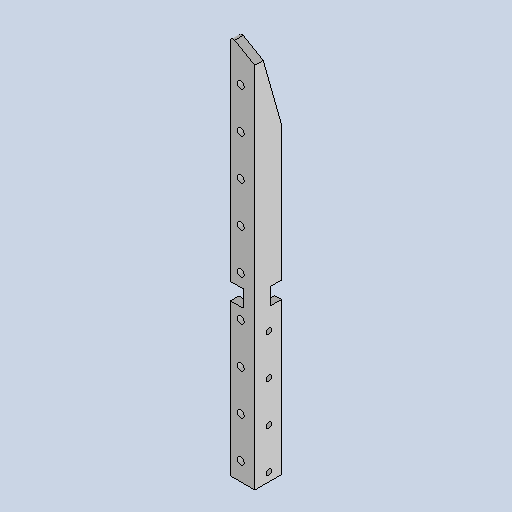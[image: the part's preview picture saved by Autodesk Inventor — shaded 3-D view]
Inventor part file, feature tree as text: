
AUTODESK INVENTOR PART (.ipt)
format: ipt  version: 2025 (Build 290162010, 162A)  size: 134,656 bytes
history: native  units: mm
features: sketch x6, other x3
ambient origin geometry x8: Origin, YZ Plane, XZ Plane, XY Plane, X Axis, Y Axis, Z Axis, Center Point
bodies: Solid1 (feature_tree)
feature tree (9):
  other  "1013.ipt"
  other  "Solid1::1013.ipt"
  other  "TaggingFeature1"
  sketch  "Sketch1"  dims[d0=10.0mm]
  sketch  "Sketch2"
  sketch  "Sketch3"
  sketch  "Sketch4"
  sketch  "Sketch5"
  sketch  "Sketch6"
